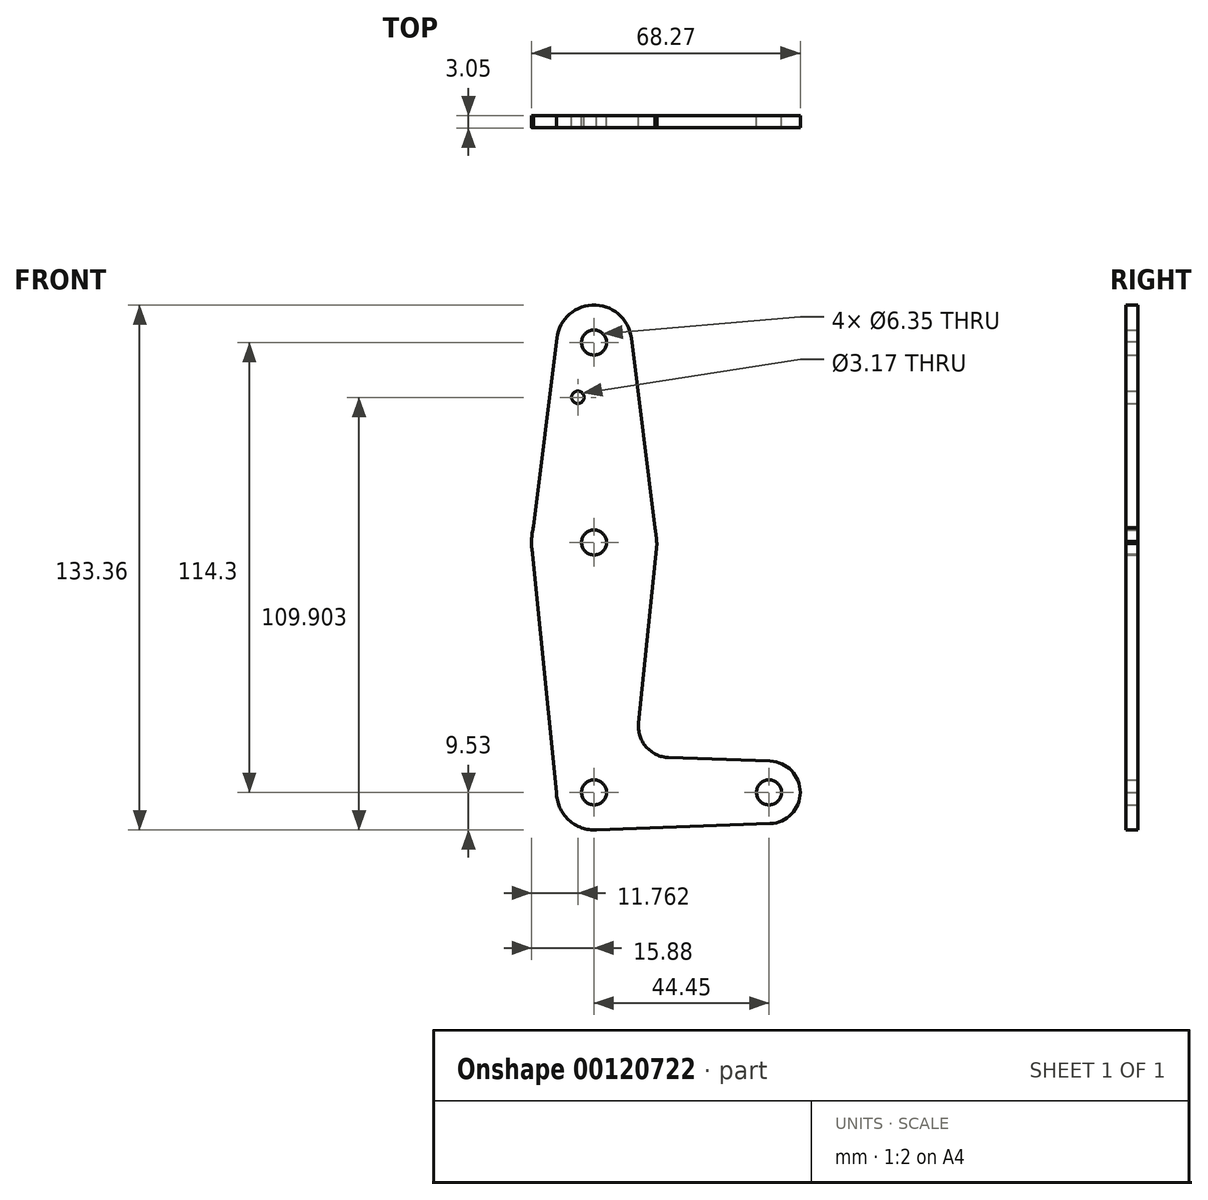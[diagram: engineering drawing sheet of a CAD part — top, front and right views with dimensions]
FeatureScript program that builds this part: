
annotation { "Feature Type Name" : "Feature", "Feature Type Description" : "" }
export const myFeature = defineFeature(function(context is Context, id is Id, definition is map)
    precondition{}
    {
        {
            var Q0;
            Q0=qCreatedBy(makeId("Front.planeOp"),FACE);
            var sketch = newSketch(context, id + "F0", { "sketchPlane" : qUnion([Q0])});
            skLineSegment(sketch, "E0", {"start": v(0, 0) * mm, "end": v(44.45, 0) * mm, "construction": true});
            skCircle(sketch, "E1", {"center": v(0, 0) * mm, "radius": 9.53 * mm});
            skCircle(sketch, "E2", {"center": v(44.45, 0) * mm, "radius": 7.94 * mm});
            skCircle(sketch, "E3", {"center": v(0, 114.3) * mm, "radius": 9.53 * mm});
            skLineSegment(sketch, "E4", {"start": v(0, 0) * mm, "end": v(0, 63.5) * mm, "construction": true});
            skLineSegment(sketch, "E5", {"start": v(0, 114.3) * mm, "end": v(0, 63.5) * mm, "construction": true});
            skCircle(sketch, "E6", {"center": v(0, 63.5) * mm, "radius": 15.88 * mm});
            skLineSegment(sketch, "E7", {"start": v(-9.52, 114.5) * mm, "end": v(-15.87, 63.28) * mm});
            skLineSegment(sketch, "E8", {"start": v(-9.53, 0) * mm, "end": v(-15.87, 63.28) * mm});
            skLineSegment(sketch, "E9", {"start": v(11.3, 17.6) * mm, "end": v(15.93, 63.28) * mm});
            skLineSegment(sketch, "E10", {"start": v(15.93, 63.28) * mm, "end": v(9.45, 115.47) * mm});
            skLineSegment(sketch, "E11", {"start": v(18.93, 8.85) * mm, "end": v(44.73, 7.93) * mm});
            skLineSegment(sketch, "E12", {"start": v(0, -9.53) * mm, "end": v(44.73, -7.93) * mm});
            skCircle(sketch, "E13", {"center": v(0, 114.3) * mm, "radius": 3.18 * mm});
            skCircle(sketch, "E14", {"center": v(0, 63.5) * mm, "radius": 3.18 * mm});
            skCircle(sketch, "E15", {"center": v(0, 0) * mm, "radius": 3.18 * mm});
            skCircle(sketch, "E16", {"center": v(44.45, 0) * mm, "radius": 3.18 * mm});
            skCircle(sketch, "E17", {"center": v(-4.12, 100.37) * mm, "radius": 1.59 * mm});
            skArc(sketch, "E18.filletArc", {"start": v(11.3, 17.6) * mm, "mid": v(13.22, 11.57) * mm, "end": v(18.93, 8.85) * mm});
            skSolve(sketch);
        }
        {
            var Q0;
            Q0 = qSketchRegion(id + "F0", true);
            extrude(context, id + "F1", {"entities" : qUnion([Q0]), "depth" : 3.05 * mm});
        }
    });
